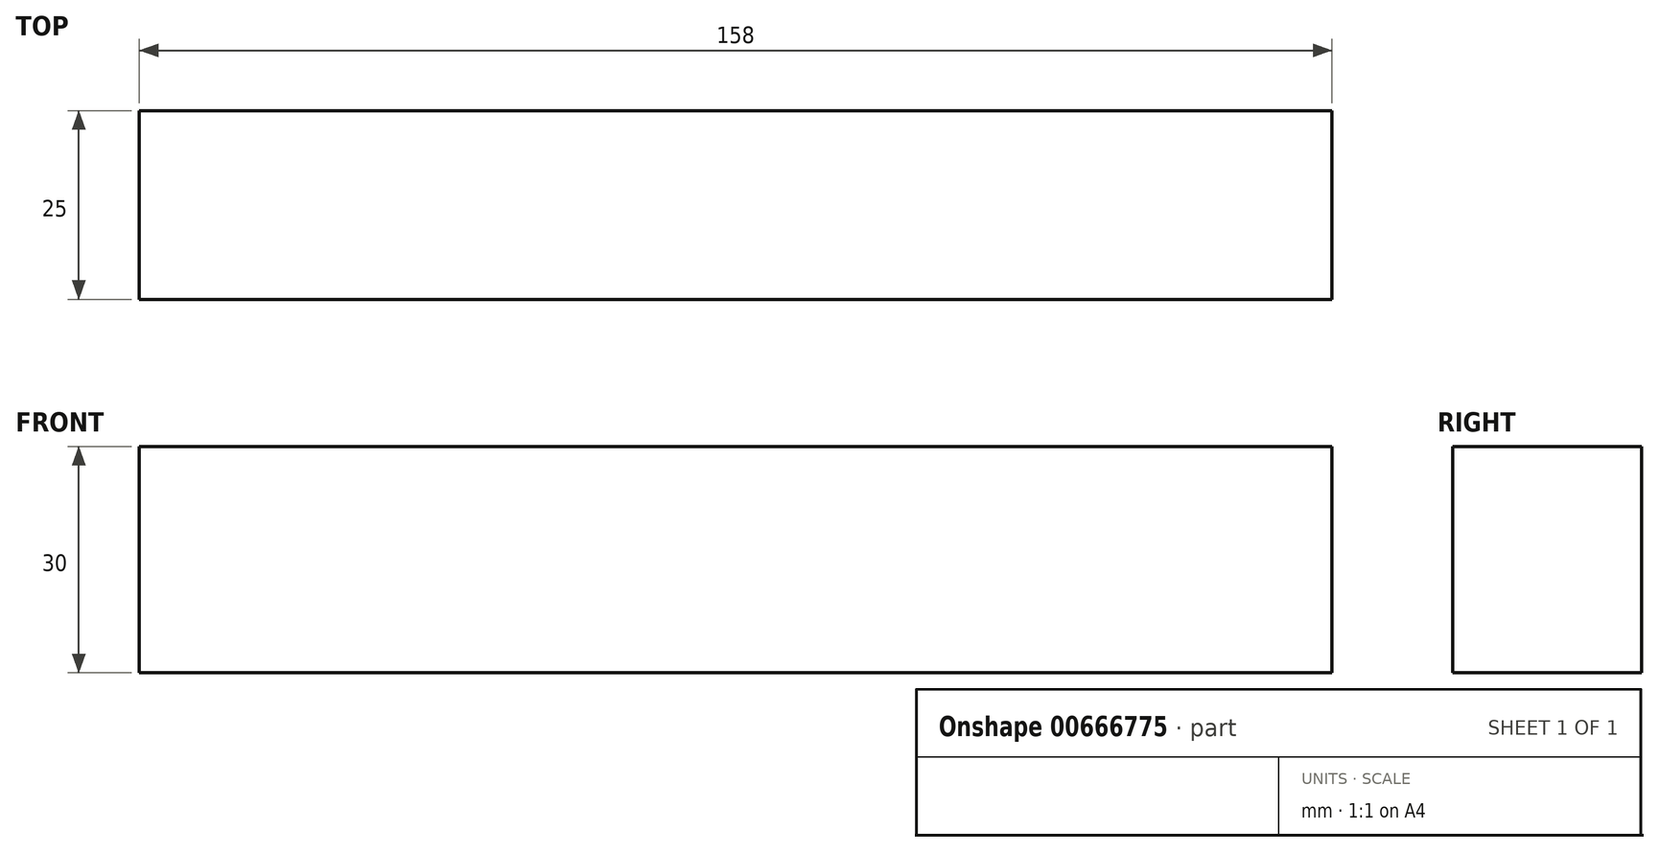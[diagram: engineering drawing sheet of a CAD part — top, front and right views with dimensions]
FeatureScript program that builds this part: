
annotation { "Feature Type Name" : "Feature", "Feature Type Description" : "" }
export const myFeature = defineFeature(function(context is Context, id is Id, definition is map)
    precondition{}
    {
        {
            var Q0;
            Q0=qCreatedBy(makeId("Front.planeOp"),FACE);
            var sketch = newSketch(context, id + "F0", { "sketchPlane" : qUnion([Q0])});
            skLineSegment(sketch, "E0.bottom", {"start": v(-79, 15) * mm, "end": v(79, 15) * mm});
            skLineSegment(sketch, "E0.top", {"start": v(-79, -15) * mm, "end": v(79, -15) * mm});
            skLineSegment(sketch, "E0.left", {"start": v(-79, 15) * mm, "end": v(-79, -15) * mm});
            skLineSegment(sketch, "E0.right", {"start": v(79, 15) * mm, "end": v(79, -15) * mm});
            skPoint(sketch, "E0.middle", {"position": v(0, 0) * mm});
            skSolve(sketch);
        }
        {
            var Q0;
            Q0 = qSketchRegion(id + "F0", true);
            extrude(context, id + "F1", {"entities" : qUnion([Q0]), "depth" : 25 * mm, "offsetDistance" : 25 * mm});
        }
    });
